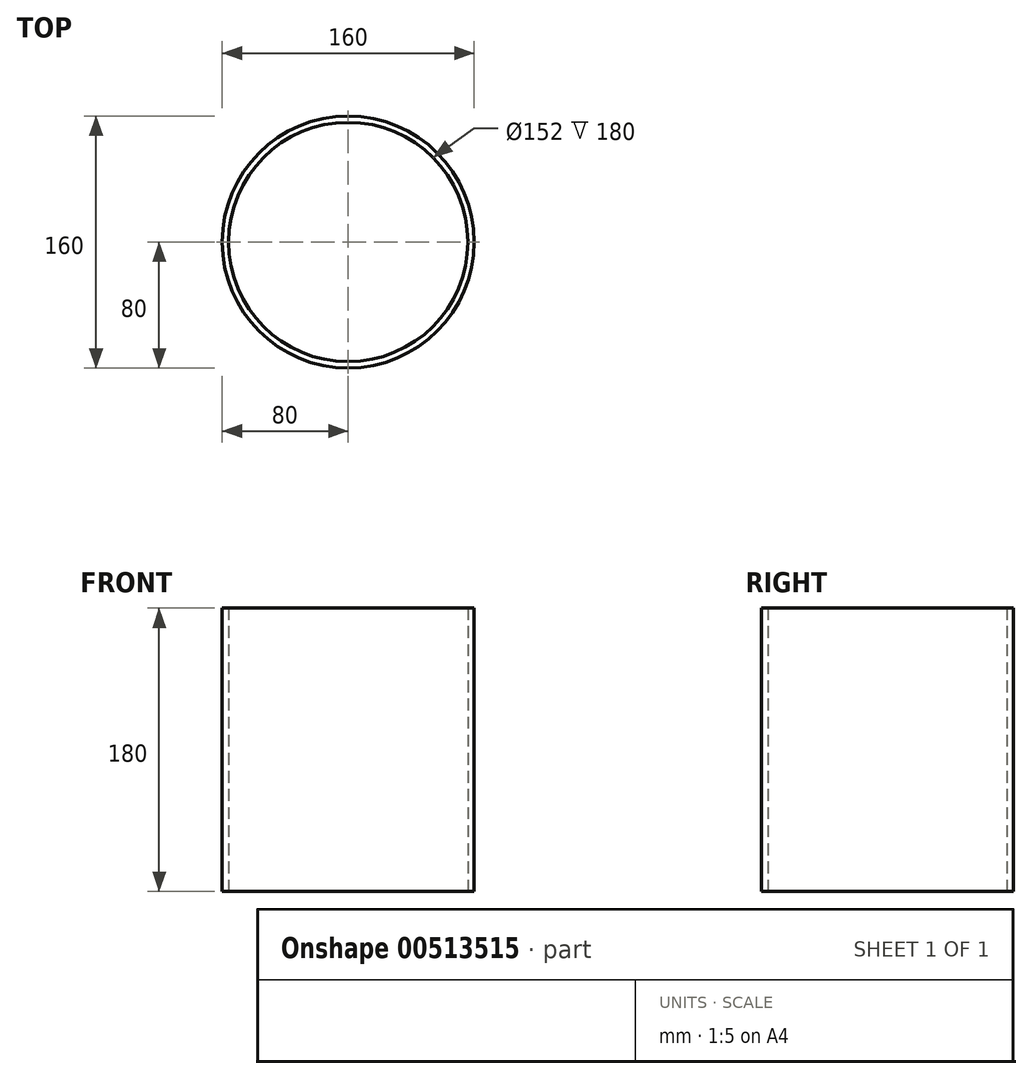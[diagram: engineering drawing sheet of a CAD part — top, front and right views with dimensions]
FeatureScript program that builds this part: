
annotation { "Feature Type Name" : "Feature", "Feature Type Description" : "" }
export const myFeature = defineFeature(function(context is Context, id is Id, definition is map)
    precondition{}
    {
        {
            var Q0;
            Q0=qCreatedBy(makeId("Top.planeOp"),FACE);
            var sketch = newSketch(context, id + "F0", { "sketchPlane" : qUnion([Q0])});
            skCircle(sketch, "E0", {"center": v(0, 0) * mm, "radius": 80 * mm});
            skCircle(sketch, "E1", {"center": v(0, 0) * mm, "radius": 76 * mm});
            skSolve(sketch);
        }
        {
            var Q0;
            Q0=makeQuery(id+"F0.imprint","IMPRINT",FACE,{"disambiguationData":[TD([[makeQuery(id+"F0.imprint","IMPRINT",EDGE,{"derivedFrom":sQuery(id+"F0.wireOp",EDGE,"E0")}),1.0]])]});
            extrude(context, id + "F1", {"entities" : qUnion([Q0]), "depth" : 180 * mm});
        }
    });
